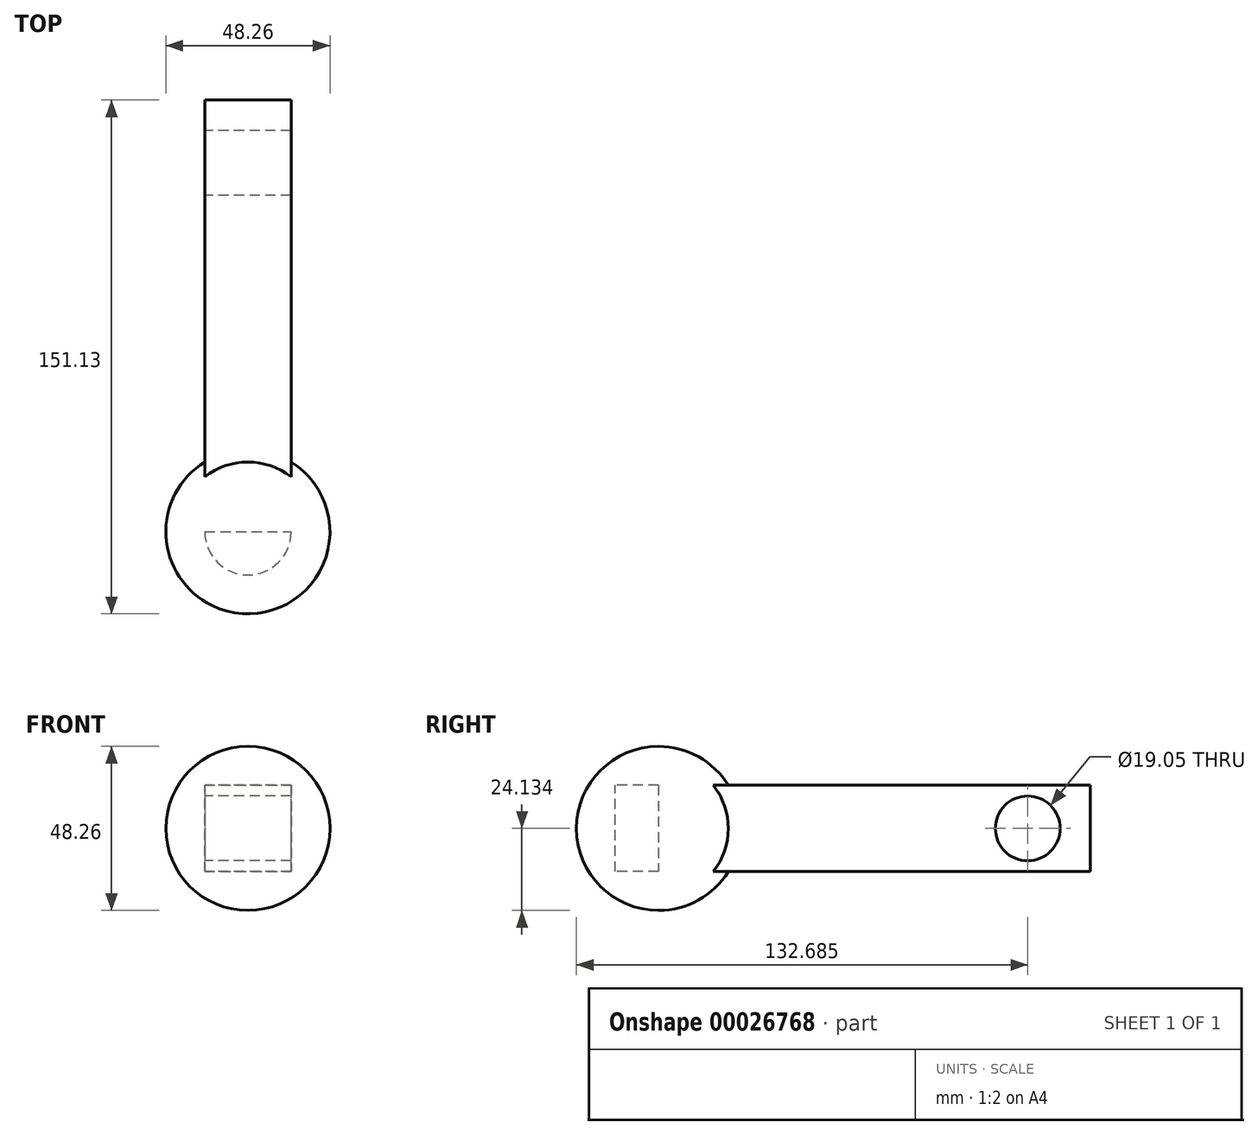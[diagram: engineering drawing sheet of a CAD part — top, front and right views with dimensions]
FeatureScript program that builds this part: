
annotation { "Feature Type Name" : "Feature", "Feature Type Description" : "" }
export const myFeature = defineFeature(function(context is Context, id is Id, definition is map)
    precondition{}
    {
        {
            var Q0;
            Q0=qCreatedBy(makeId("Front.planeOp"),FACE);
            var sketch = newSketch(context, id + "F0", { "sketchPlane" : qUnion([Q0])});
            skLineSegment(sketch, "E0.bottom", {"start": v(-59.13, -26.7) * mm, "end": v(-33.73, -26.7) * mm});
            skLineSegment(sketch, "E0.top", {"start": v(-59.13, -52.1) * mm, "end": v(-33.73, -52.1) * mm});
            skLineSegment(sketch, "E0.left", {"start": v(-59.13, -26.7) * mm, "end": v(-59.13, -52.1) * mm});
            skLineSegment(sketch, "E0.right", {"start": v(-33.73, -26.7) * mm, "end": v(-33.73, -52.1) * mm});
            skSolve(sketch);
        }
        {
            var Q0;
            Q0=makeQuery(id+"F0.imprint","IMPRINT",FACE,{"disambiguationData":[TD([[makeQuery(id+"F0.imprint","IMPRINT",EDGE,{"derivedFrom":sQuery(id+"F0.wireOp",EDGE,"E0.bottom")}),-1.0]])]});
            extrude(context, id + "F1", {"entities" : qUnion([Q0]), "depth" : 127 * mm});
        }
        {
            var Q0;
            Q0=makeQuery(id+"F1.opExtrude","CAP_FACE",FACE,{"disambiguationData":[OSD([sQuery(id+"F0.wireOp",EDGE,"E0.bottom"),sQuery(id+"F0.wireOp",EDGE,"E0.top"),sQuery(id+"F0.wireOp",EDGE,"E0.left"),sQuery(id+"F0.wireOp",EDGE,"E0.right")])],"isStart":false});
            var sketch = newSketch(context, id + "F2", { "sketchPlane" : qUnion([Q0])});
            skArc(sketch, "E1", {"start": v(-46.43, -15.28) * mm, "mid": v(-70.56, -39.4) * mm, "end": v(-46.43, -63.54) * mm});
            skPoint(sketch, "E2", {"position": v(-46.43, -15.28) * mm});
            skPoint(sketch, "E3", {"position": v(-46.43, -63.54) * mm});
            skLineSegment(sketch, "E4", {"start": v(-46.43, -15.28) * mm, "end": v(-46.43, -63.54) * mm});
            skSolve(sketch);
        }
        {
            var Q0;
            Q0=makeQuery(id+"F2.imprint","IMPRINT",FACE,{"disambiguationData":[TD([[makeQuery(id+"F2.imprint","IMPRINT",EDGE,{"derivedFrom":sQuery(id+"F2.wireOp",EDGE,"E1")}),1.0]])]});
            var Q1;
            Q1=sQuery(id+"F2.wireOp",EDGE,"E4");
            revolve(context, id + "F3", {"operationType" : NewBodyOperationType.ADD, "entities" : qUnion([Q0]), "axis" : qUnion([Q1]), "revolveType" : RevolveType.FULL});
        }
        {
            var Q0;
            Q0=makeQuery(id+"F1.opExtrude","SWEPT_FACE",FACE,{"disambiguationData":[OSD([sQuery(id+"F0.wireOp",EDGE,"E0.left")])]});
            var sketch = newSketch(context, id + "F4", { "sketchPlane" : qUnion([Q0])});
            skCircle(sketch, "E5", {"center": v(18.45, -39.4) * mm, "radius": 9.53 * mm});
            skSolve(sketch);
        }
        {
            var Q0;
            Q0=makeQuery(id+"F4.imprint","IMPRINT",FACE,{"disambiguationData":[TD([[makeQuery(id+"F4.imprint","IMPRINT",EDGE,{"derivedFrom":sQuery(id+"F4.wireOp",EDGE,"E5")}),1.0]])]});
            extrude(context, id + "F5", {"entities" : qUnion([Q0]), "operationType" : NewBodyOperationType.REMOVE, "endBound" : BoundingType.THROUGH_ALL, "oppositeDirection" : true, "depth" : 25.4 * mm});
        }
    });
